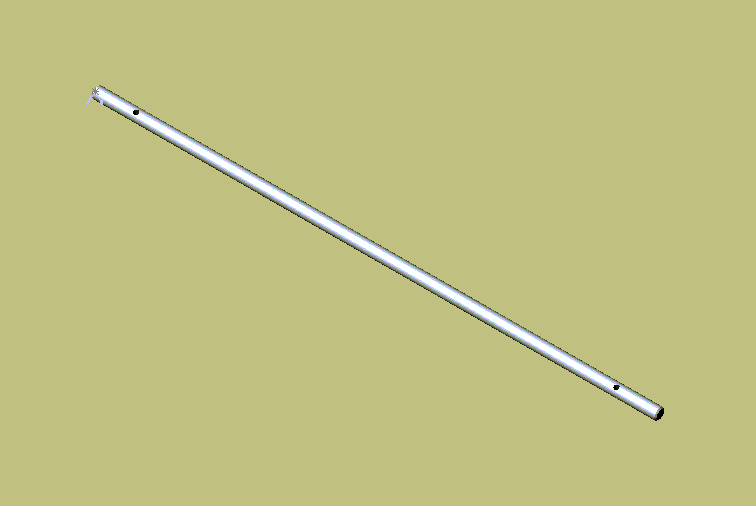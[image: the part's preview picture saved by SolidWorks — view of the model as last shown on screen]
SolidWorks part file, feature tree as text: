
SOLIDWORKS PART (.sldprt)
format: sldprt  version: not decoded by parser v0  size: 110,080 bytes
history: native  units: mm
features: plane x3, sketch x2, material x1, extrude x1, chamfer x1, cut_extrude x1 (+8 scaffold rows collapsed)
feature tree (17):
  scaffold x8  (default folders/planes/origin — collapsed)
  material  "Matériau <non spécifié>"
  plane  "Plane1"
  plane  "Plane2"
  plane  "Plane3"
  sketch  "Esquisse1"  dims[D1=5.0mm]
  extrude  "Base-Extrusion"  Depth=228mm
  chamfer  "Chanfrein1"  Distance=0.5mm Angle=45deg
  sketch  "Esquisse2"  dims[D1=2.0mm D4=2.0mm D2=17.0mm D3=17.0mm]
  cut_extrude  "Enlèv. mat.-Extru.1"  Depth=100mm
decode coverage: 5 of 5 modeling features carry decoded parameters
note: suppression state not decoded; provenance and decode notes live in map.json
